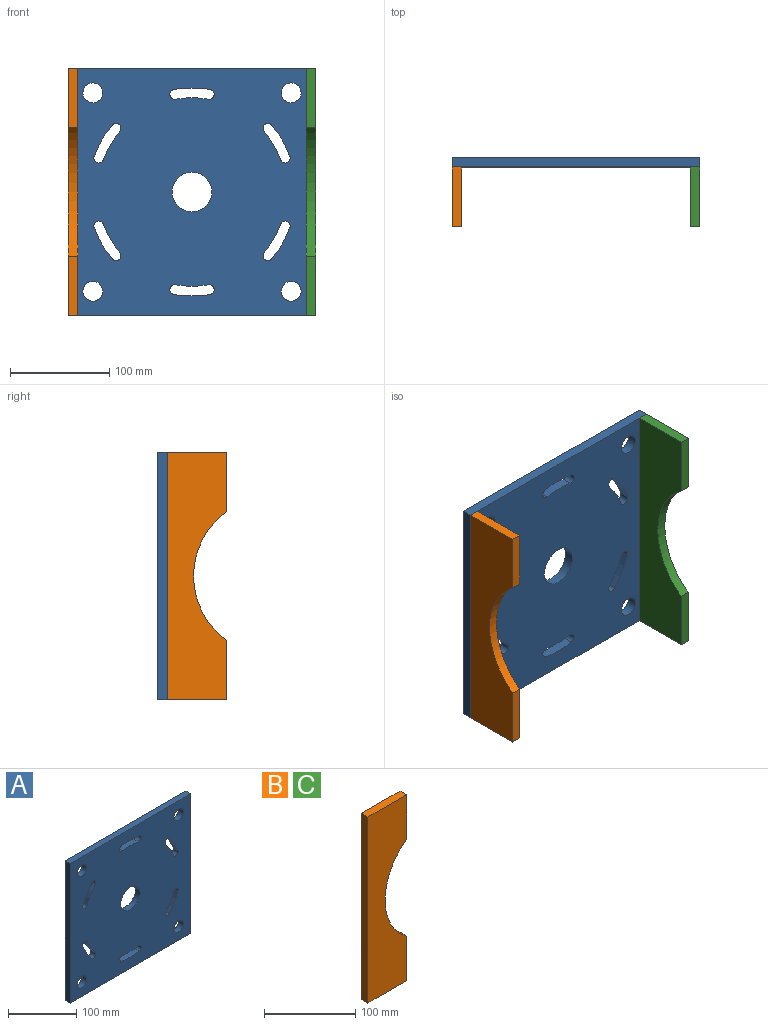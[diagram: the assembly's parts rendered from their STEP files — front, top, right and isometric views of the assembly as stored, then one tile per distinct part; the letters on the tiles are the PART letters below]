
ASSEMBLY  parts=3 mates=1
PART A: 35 faces, bbox 250x10x250 mm
  f0: cylinder r=5mm len=10mm, axis (0,1,0), area 157.1mm2, adj f1,f32,f33,f34
  f1: cylinder r=95mm len=28.57mm, axis (0,1,0), area 331.6mm2, adj f0,f2,f33,f34
  f2: cylinder r=5mm len=10mm, axis (0,1,0), area 157.1mm2, adj f1,f32,f33,f34
  f3: cylinder r=5mm len=10mm, axis (0,1,0), area 157.1mm2, adj f4,f21,f33,f34
  f4: cylinder r=95mm len=28.57mm, axis (0,1,0), area 331.6mm2, adj f3,f5,f33,f34
  f5: cylinder r=5mm len=10mm, axis (0,1,0), area 157.1mm2, adj f4,f21,f33,f34
  f6: cylinder r=5mm len=10mm, axis (0,1,0), area 157.1mm2, adj f7,f22,f33,f34
  f7: cylinder r=95mm len=32.99mm, axis (0,1,0), area 331.6mm2, adj f6,f8,f33,f34
  f8: cylinder r=5mm len=10mm, axis (0,1,0), area 157.1mm2, adj f7,f22,f33,f34
  f9: cylinder r=5mm len=10mm, axis (0,1,0), area 157.1mm2, adj f10,f23,f33,f34
  f10: cylinder r=95mm len=28.57mm, axis (0,1,0), area 331.6mm2, adj f9,f11,f33,f34
  f11: cylinder r=5mm len=10mm, axis (0,1,0), area 157.1mm2, adj f10,f23,f33,f34
  f12: cylinder r=5mm len=10mm, axis (0,1,0), area 157.1mm2, adj f13,f24,f33,f34
  f13: cylinder r=95mm len=28.57mm, axis (0,1,0), area 331.6mm2, adj f12,f14,f33,f34
  f14: cylinder r=5mm len=10mm, axis (0,1,0), area 157.1mm2, adj f13,f24,f33,f34
  f15: cylinder r=105mm len=36.47mm, axis (0,1,0), area 366.5mm2, adj f16,f30,f33,f34
  f16: cylinder r=5mm len=10mm, axis (0,1,0), area 157.1mm2, adj f15,f17,f33,f34
  f17: cylinder r=95mm len=32.99mm, axis (0,1,0), area 331.6mm2, adj f16,f30,f33,f34
  f18: plane 250x10mm, normal (1,0,0), area 2500mm2, adj f19,f31,f33,f34
  f19: plane 250x10mm, normal (0,0,1), area 2500mm2, adj f18,f20,f33,f34
  f20: plane 250x10mm, normal (-1,0,0), area 2500mm2, adj f19,f31,f33,f34
  f21: cylinder r=105mm len=31.58mm, axis (0,1,0), area 366.5mm2, adj f3,f5,f33,f34
  f22: cylinder r=105mm len=36.47mm, axis (0,1,0), area 366.5mm2, adj f6,f8,f33,f34
  f23: cylinder r=105mm len=31.58mm, axis (0,1,0), area 366.5mm2, adj f9,f11,f33,f34
  f24: cylinder r=105mm len=31.58mm, axis (0,1,0), area 366.5mm2, adj f12,f14,f33,f34
  f25: cylinder r=10mm len=20mm, axis (0,1,0), area 628.3mm2, adj f33,f34
  f26: cylinder r=10mm len=20mm, axis (0,1,0), area 628.3mm2, adj f33,f34
  f27: cylinder r=10mm len=20mm, axis (0,1,0), area 628.3mm2, adj f33,f34
  f28: cylinder r=10mm len=20mm, axis (0,1,0), area 628.3mm2, adj f33,f34
  f29: cylinder r=20mm len=40mm, axis (0,1,0), area 1256.6mm2, adj f33,f34
  f30: cylinder r=5mm len=10mm, axis (0,1,0), area 157.1mm2, adj f15,f17,f33,f34
  f31: plane 250x10mm, normal (0,0,-1), area 2500mm2, adj f18,f20,f33,f34
  f32: cylinder r=105mm len=31.58mm, axis (0,1,0), area 366.5mm2, adj f0,f2,f33,f34
  f33: plane 250x250mm, normal (0,-1,0), area 57421.1mm2, adj f0,f1,f2,f3,f4,f5,f6,f7
  f34: plane 250x250mm, normal (0,1,0), area 57421.1mm2, adj f0,f1,f2,f3,f4,f5,f6,f7
PART B: 8 faces, bbox 60x10x250 mm
  f0: plane 60x10mm, normal (0,0,1), area 600mm2, adj f1,f5,f6,f7
  f1: plane 250x10mm, normal (-1,0,0), area 2500mm2, adj f0,f2,f6,f7
  f2: plane 60x10mm, normal (0,0,-1), area 600mm2, adj f1,f3,f6,f7
  f3: plane 60x10mm, normal (1,0,0), area 600mm2, adj f2,f4,f6,f7
  f4: cylinder r=80mm len=130mm, axis (0,1,0), area 1517.5mm2, adj f3,f5,f6,f7
  f5: plane 60x10mm, normal (1,0,0), area 600mm2, adj f0,f4,f6,f7
  f6: plane 250x60mm, normal (0,-1,0), area 11961.5mm2, adj f0,f1,f2,f3,f4,f5
  f7: plane 250x60mm, normal (0,1,0), area 11961.5mm2, adj f0,f1,f2,f3,f4,f5
PART C: same geometry as B
PLACE A t=(-90.91,49.19,-77.96)mm
PLACE B rot(axis=(0,0,-1),90deg) t=(-205.91,39.19,-91.19)mm
PLACE C rot(axis=(-0.71,0.71,0),180deg) t=(24.09,39.19,-64.73)mm
MATE slider C.f2 <-> A.f19  axis (0,0,-1) through (34.09,39.19,47.04)mm
